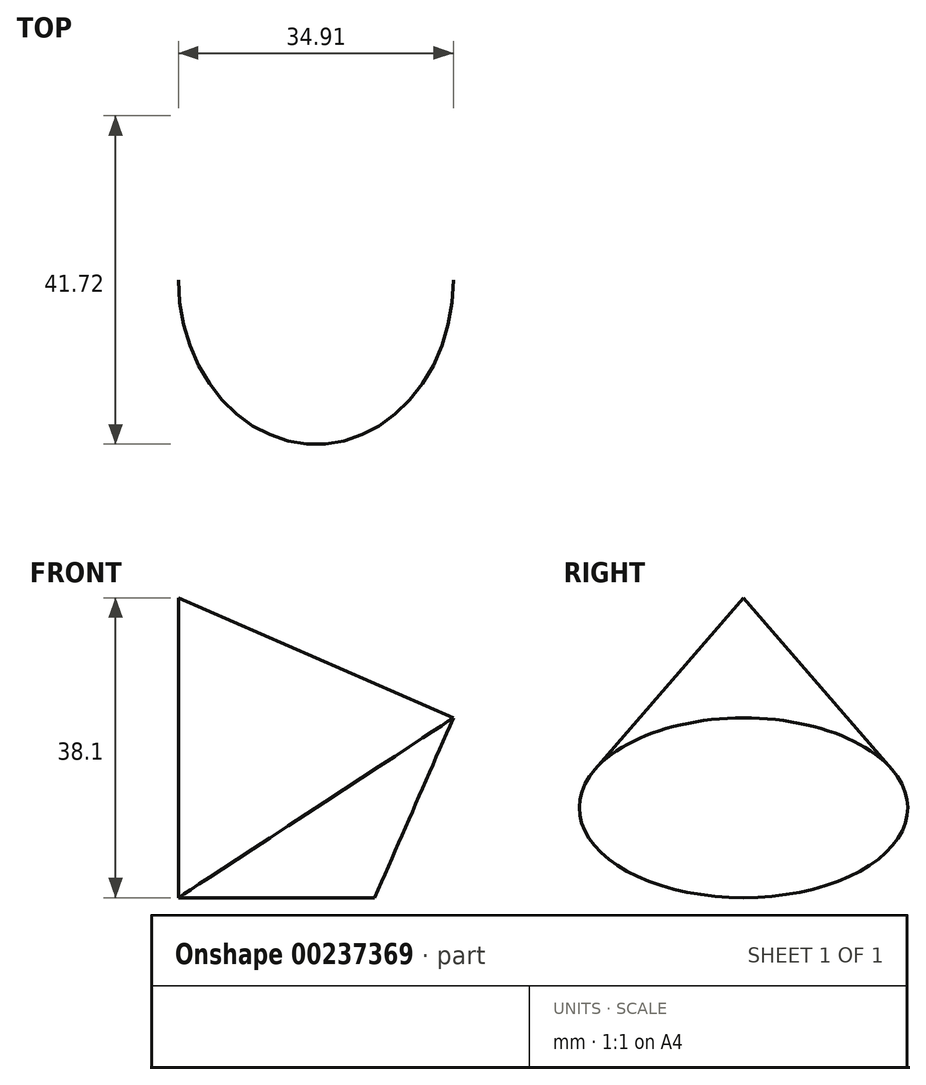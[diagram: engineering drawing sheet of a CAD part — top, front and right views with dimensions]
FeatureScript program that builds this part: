
annotation { "Feature Type Name" : "Feature", "Feature Type Description" : "" }
export const myFeature = defineFeature(function(context is Context, id is Id, definition is map)
    precondition{}
    {
        {
            var Q0;
            Q0=qCreatedBy(makeId("Front.planeOp"),FACE);
            var sketch = newSketch(context, id + "F0", { "sketchPlane" : qUnion([Q0])});
            skLineSegment(sketch, "E0", {"start": v(0, 0) * mm, "end": v(0, 38.1) * mm});
            skLineSegment(sketch, "E1", {"start": v(0, 0) * mm, "end": v(24.92, 0) * mm});
            skLineSegment(sketch, "E2", {"start": v(0, 38.1) * mm, "end": v(24.92, 0) * mm});
            skSolve(sketch);
        }
        {
            var Q0;
            Q0=makeQuery(id+"F0.imprint","IMPRINT",FACE,{"disambiguationData":[TD([[makeQuery(id+"F0.imprint","IMPRINT",EDGE,{"derivedFrom":sQuery(id+"F0.wireOp",EDGE,"E0")}),-1.0]])]});
            var Q1;
            Q1=sQuery(id+"F0.wireOp",EDGE,"E2");
            revolve(context, id + "F1", {"entities" : qUnion([Q0]), "axis" : qUnion([Q1]), "revolveType" : RevolveType.FULL});
        }
    });
